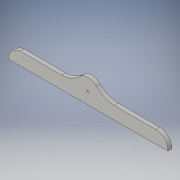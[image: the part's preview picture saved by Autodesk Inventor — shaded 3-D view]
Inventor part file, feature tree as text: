
AUTODESK INVENTOR PART (.ipt)
format: ipt  version: 2016 (Build 200138000, 138)  size: 237,568 bytes
history: native  units: in
note: dims shown in document units (in); Inventor stores cm internally (conversion verified against a paired STEP export)
features: extrude x1, hole x1, sketch x1
ambient origin geometry x8: Origin, YZ Plane, XZ Plane, XY Plane, X Axis, Y Axis, Z Axis, Center Point
bodies: Body1 (feature_tree)
feature tree (3):
  extrude  "Extrusion2"  Depth=0.25in TaperAngle=0.0deg
  hole  "Hole3"  [1 undecoded]
  sketch  "Sketch1"  dims[d2=0.76in d13=0.25in d14=0.0in d58=0.76in d62=0.1in d63=0.75in d64=0.375in d65=0.25in d66=0.5635in d67=0.1in d68=0.8108in d74=10.0in d75=0.8in d76=1.5in d78=1.6727in d79=0.7328in d87=0.75in d89=2.6in d90=2.6in d91=0.8669in d92=0.7584in d93=0.8603in d36=1.0in d37=1.0in]
note: 1 required parameter value undecoded (feature->parameter linkage not recoverable at this tier; creation-order binding heuristic only, values carry confidence <= 0.55)
